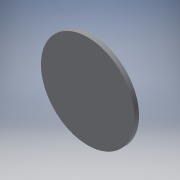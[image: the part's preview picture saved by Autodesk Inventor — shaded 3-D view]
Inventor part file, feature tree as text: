
AUTODESK INVENTOR PART (.ipt)
format: ipt  version: 2016 (Build 200138000, 138)  size: 87,552 bytes
history: native  units: in
note: dims shown in document units (in); Inventor stores cm internally (conversion verified against a paired STEP export)
features: extrude x1, sketch x1, reference x1
ambient origin geometry x8: Origin, YZ Plane, XZ Plane, XY Plane, X Axis, Y Axis, Z Axis, Center Point
bodies: Solid1 (feature_tree)
feature tree (3):
  extrude  "Extrusion1"  Depth=0.0394in TaperAngle=0.0deg
  sketch  "Sketch1"  dims[d0=0.7874in d1=0.0394in d2=0.0in]
  reference  "Reference1"
